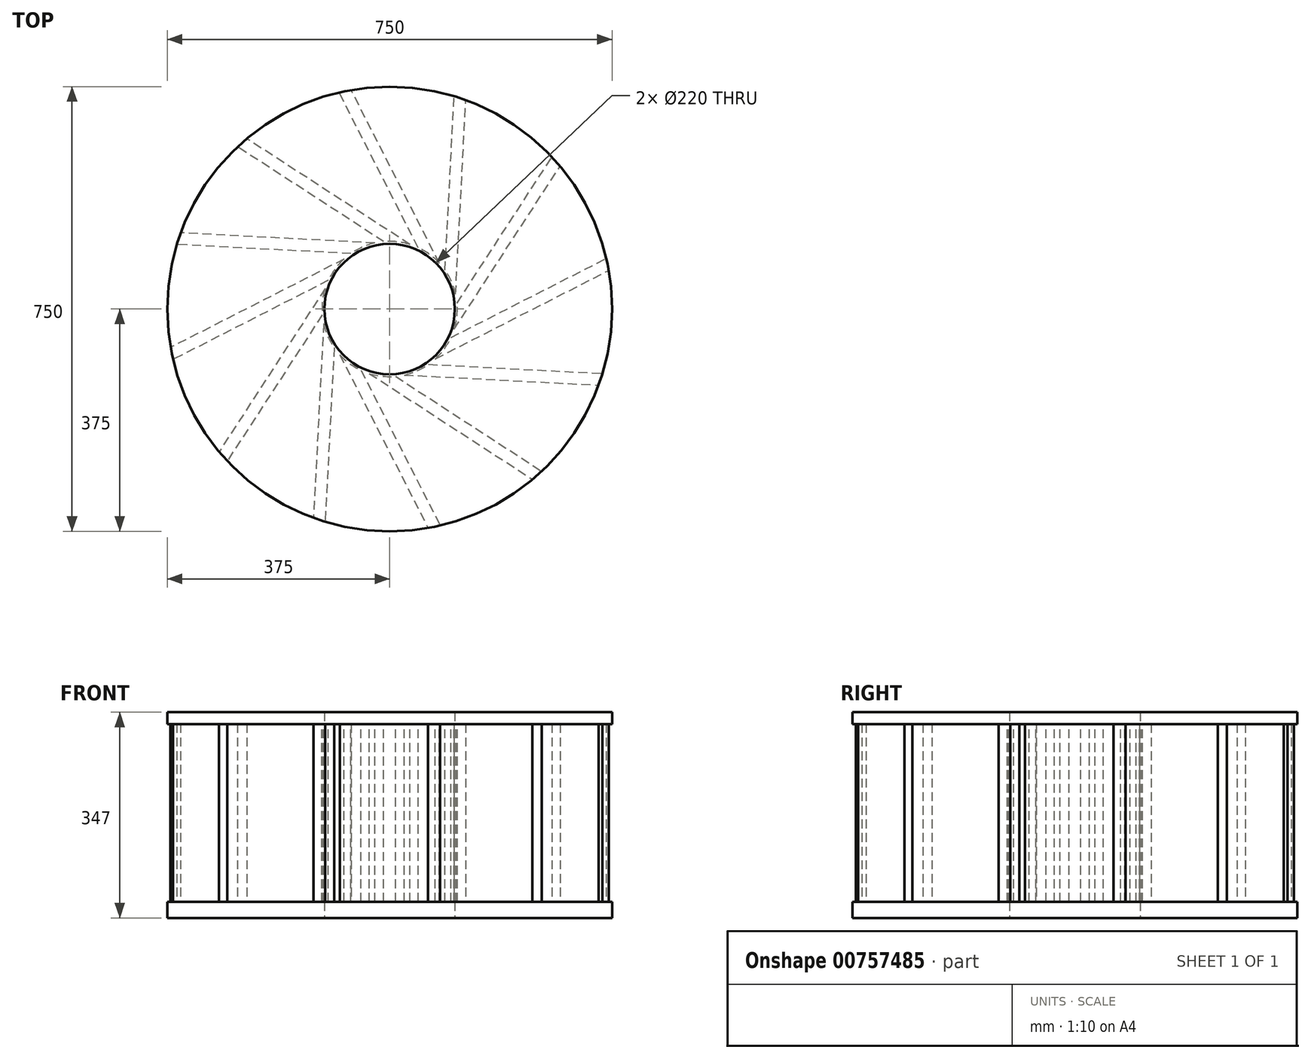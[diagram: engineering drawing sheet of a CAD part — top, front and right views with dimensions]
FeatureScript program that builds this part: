
annotation { "Feature Type Name" : "Feature", "Feature Type Description" : "" }
export const myFeature = defineFeature(function(context is Context, id is Id, definition is map)
    precondition{}
    {
        {
            var Q0;
            Q0=qCreatedBy(makeId("Top.planeOp"),FACE);
            var sketch = newSketch(context, id + "F0", { "sketchPlane" : qUnion([Q0])});
            skCircle(sketch, "E0", {"center": v(0, 0) * mm, "radius": 375 * mm});
            skCircle(sketch, "E1", {"center": v(0, 0) * mm, "radius": 110 * mm});
            skSolve(sketch);
        }
        {
            var Q0;
            Q0 = qSketchRegion(id + "F0", true);
            extrude(context, id + "F1", {"entities" : qUnion([Q0]), "depth" : 2 * mm, "offsetDistance" : 25 * mm});
        }
        {
            var Q0;
            Q0=makeQuery(id+"F1.opExtrude","CAP_FACE",FACE,{"disambiguationData":[OSD([sQuery(id+"F0.wireOp",EDGE,"E0"),sQuery(id+"F0.wireOp",EDGE,"E1")])],"isStart":false});
            extrude(context, id + "F2", {"entities" : qUnion([Q0]), "operationType" : NewBodyOperationType.ADD, "depth" : 25 * mm, "offsetDistance" : 25 * mm});
        }
        {
            var Q0;
            Q0=makeQuery(id+"F2.opExtrude","CAP_FACE",FACE,{"disambiguationData":[OSD([sQuery(id+"F0.wireOp",EDGE,"E0"),sQuery(id+"F0.wireOp",EDGE,"E1")])],"isStart":false});
            var sketch = newSketch(context, id + "F3", { "sketchPlane" : qUnion([Q0])});
            skCircle(sketch, "E2.0", {"center": v(0, 0) * mm, "radius": 375 * mm});
            skCircle(sketch, "E3.0", {"center": v(0, 0) * mm, "radius": 110 * mm});
            skLineSegment(sketch, "E4", {"start": v(0, 110) * mm, "end": v(-352.3, 128.46) * mm});
            skLineSegment(sketch, "E5", {"start": v(-58.67, 93.05) * mm, "end": v(-358.88, 108.78) * mm});
            skLineSegment(sketch, "E6", {"start": v(-375, 0) * mm, "end": v(375, 0) * mm, "construction": true});
            skSolve(sketch);
        }
        {
            var Q0;
            {var subQ0=sQuery(id+"F3.wireOp",EDGE,"E4");Q0=makeQuery(id+"F3.imprint","IMPRINT",FACE,{"disambiguationData":[TD([[makeQuery(id+"F3.imprint","IMPRINT",EDGE,{"derivedFrom":subQ0}),1.0]])]});}
            extrude(context, id + "F4", {"entities" : qUnion([Q0]), "depth" : 300 * mm, "offsetDistance" : 25 * mm});
        }
        {
            var Q0;
            Q0=qCreatedBy(makeId("Right.planeOp"),FACE);
            var sketch = newSketch(context, id + "F5", { "sketchPlane" : qUnion([Q0])});
            skLineSegment(sketch, "E7", {"start": v(0, 54.53) * mm, "end": v(0, -122.25) * mm, "construction": true});
            skSolve(sketch);
        }
        {
            var Q0;
            Q0=makeQuery(id+"F4.opExtrude","SWEPT_BODY",BODY,{"disambiguationData":[OSD([sQuery(id+"F3.wireOp",EDGE,"E2.0"),sQuery(id+"F3.wireOp",EDGE,"E3.0"),sQuery(id+"F3.wireOp",EDGE,"E4"),sQuery(id+"F3.wireOp",EDGE,"E5")])]});
            var Q1;
            Q1=sQuery(id+"F5.wireOp",EDGE,"E7");
            circularPattern(context, id + "F6", {"entities" : qUnion([Q0]), "axis" : qUnion([Q1]), "angle" : 360 * degree, "instanceCount" : 12, "equalSpace" : true, "isCentered" : true});
        }
        {
            var Q0;
            Q0=makeQuery(id+"F4.opExtrude","CAP_FACE",FACE,{"disambiguationData":[OSD([sQuery(id+"F3.wireOp",EDGE,"E2.0"),sQuery(id+"F3.wireOp",EDGE,"E3.0"),sQuery(id+"F3.wireOp",EDGE,"E4"),sQuery(id+"F3.wireOp",EDGE,"E5")])],"isStart":false});
            var sketch = newSketch(context, id + "F7", { "sketchPlane" : qUnion([Q0])});
            skLineSegment(sketch, "E8", {"start": v(-24.78, 111.3) * mm, "end": v(-19.33, 119.69) * mm, "construction": true});
            skCircle(sketch, "E9", {"center": v(0, 0) * mm, "radius": 114.02 * mm});
            skSolve(sketch);
        }
        {
            var Q0;
            {var subQ5=makeQuery(id+"F4.opExtrude","CAP_EDGE",EDGE,{"disambiguationData":[OSD([sQuery(id+"F3.wireOp",EDGE,"E3.0")])],"isStart":false});Q0=makeQuery(id+"F7.imprint","IMPRINT",FACE,{"disambiguationData":[TD([[makeQuery(id+"F7.imprint","IMPRINT",EDGE,{"derivedFrom":subQ5}),1.0]])]});}
            var Q1;
            {var subQ5=makeQuery(id+"F4.opExtrude","CAP_EDGE",EDGE,{"disambiguationData":[OSD([sQuery(id+"F3.wireOp",EDGE,"E3.0")])],"isStart":false});Q1=makeQuery(id+"F7.imprint","IMPRINT",FACE,{"disambiguationData":[TD([[makeQuery(id+"F7.imprint","IMPRINT",EDGE,{"derivedFrom":subQ5}),-1.0]])]});}
            var Q2;
            Q2=makeQuery(id+"F2.opExtrude","CAP_FACE",FACE,{"disambiguationData":[OSD([sQuery(id+"F0.wireOp",EDGE,"E0"),sQuery(id+"F0.wireOp",EDGE,"E1")])],"isStart":false});
            extrude(context, id + "F8", {"entities" : qUnion([Q0, Q1]), "operationType" : NewBodyOperationType.REMOVE, "endBound" : BoundingType.UP_TO_SURFACE, "oppositeDirection" : true, "depth" : 25 * mm, "endBoundEntityFace" : qUnion([Q2]), "offsetDistance" : 25 * mm});
        }
        {
            var Q0;
            Q0=makeQuery(id+"F6.opPattern","COPY",FACE,{"derivedFrom":makeQuery(id+"F4.opExtrude","CAP_FACE",FACE,{"disambiguationData":[OSD([sQuery(id+"F3.wireOp",EDGE,"E2.0"),sQuery(id+"F3.wireOp",EDGE,"E3.0"),sQuery(id+"F3.wireOp",EDGE,"E4"),sQuery(id+"F3.wireOp",EDGE,"E5")])],"isStart":false}),"instanceName":"-3"});
            var sketch = newSketch(context, id + "F9", { "sketchPlane" : qUnion([Q0])});
            skCircle(sketch, "E10.0", {"center": v(0, 0) * mm, "radius": 375 * mm});
            skCircle(sketch, "E11.0", {"center": v(0, 0) * mm, "radius": 110 * mm});
            skSolve(sketch);
        }
        {
            var Q0;
            Q0 = qSketchRegion(id + "F9", true);
            extrude(context, id + "F10", {"entities" : qUnion([Q0]), "depth" : 20 * mm, "offsetDistance" : 25 * mm});
        }
    });
